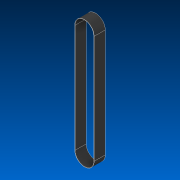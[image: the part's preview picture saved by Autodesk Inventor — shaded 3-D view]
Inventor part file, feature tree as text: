
AUTODESK INVENTOR PART (.ipt)
format: ipt  version: 2022.2 (Build 262287000, 287)  size: 92,160 bytes
history: native  units: in
note: dims shown in document units (in); Inventor stores cm internally (conversion verified against a paired STEP export)
features: extrude x1, sketch x1
ambient origin geometry x8: Origin, YZ Plane, XZ Plane, XY Plane, X Axis, Y Axis, Z Axis, Center Point
bodies: Solid1 (feature_tree)
feature tree (2):
  extrude  "Extrusion1"  Depth=1.75in
  sketch  "Sketch1"  dims[d0=19.5in d1=1.75in d2=0.0625in d3=2.0in d4=0.0in]
